SOLIDWORKS PART (.sldprt)
format: sldprt  version: not decoded by parser v0  size: 221,184 bytes
history: native  units: mm
features: sketch x8, extrude x8, fillet x3, chamfer x2, material x1 (+13 scaffold rows collapsed)
feature tree (35):
  scaffold x13  (default folders/planes/origin — collapsed)
  material  "Material <not specified>"
  sketch  "Sketch1"  dims[c1.D15=4.0mm c1.D1=32.0mm c1.D2=28.0mm c1.D3=2.0mm c1.D4=2.0mm c1.D5=2.0mm c2.D3=2.0mm c2.D6=2.0mm c2.D7=2.0mm c2.D8=15.0mm c2.D9=15.0mm c2.D10=2.0mm c2.D11=3.0mm c2.D12=19.0mm c2.D13=12.0mm c2.D14=10.0mm]
  extrude  "Boss-Extrude1"  Depth=23mm
  fillet  "Fillet1"  Radius=5mm
  sketch  "Sketch2"  dims[D1=32.0mm]
  extrude  "Boss-Extrude2"  Depth=508mm
  fillet  "Fillet2"  Radius=1mm
  sketch  "Sketch4"  dims[D1=35.0mm]
  extrude  "Boss-Extrude3"  Depth=29mm
  chamfer  "Chamfer1"  Distance=3.5mm Angle=45deg
  sketch  "Sketch5"  dims[D1=0.0mm]
  extrude  "Boss-Extrude4"  Depth=508mm
  sketch  "Sketch6"  dims[D1=29.0mm]
  extrude  "Boss-Extrude5"  Depth=34mm
  chamfer  "Chamfer2"  Distance=3.5mm Angle=45deg
  sketch  "Sketch7"  dims[D1=26.0mm]
  extrude  "Boss-Extrude6"  Depth=8mm
  sketch  "Sketch8"  dims[D1=6.35mm]
  extrude  "Boss-Extrude7"  Depth=12mm
  sketch  "Sketch9"  dims[D1=23.0mm]
  extrude  "Boss-Extrude8"  Depth=12mm
  fillet  "Fillet3"  Radius=9mm
decode coverage: 21 of 21 modeling features carry decoded parameters
note: suppression state not decoded; provenance and decode notes live in map.json
